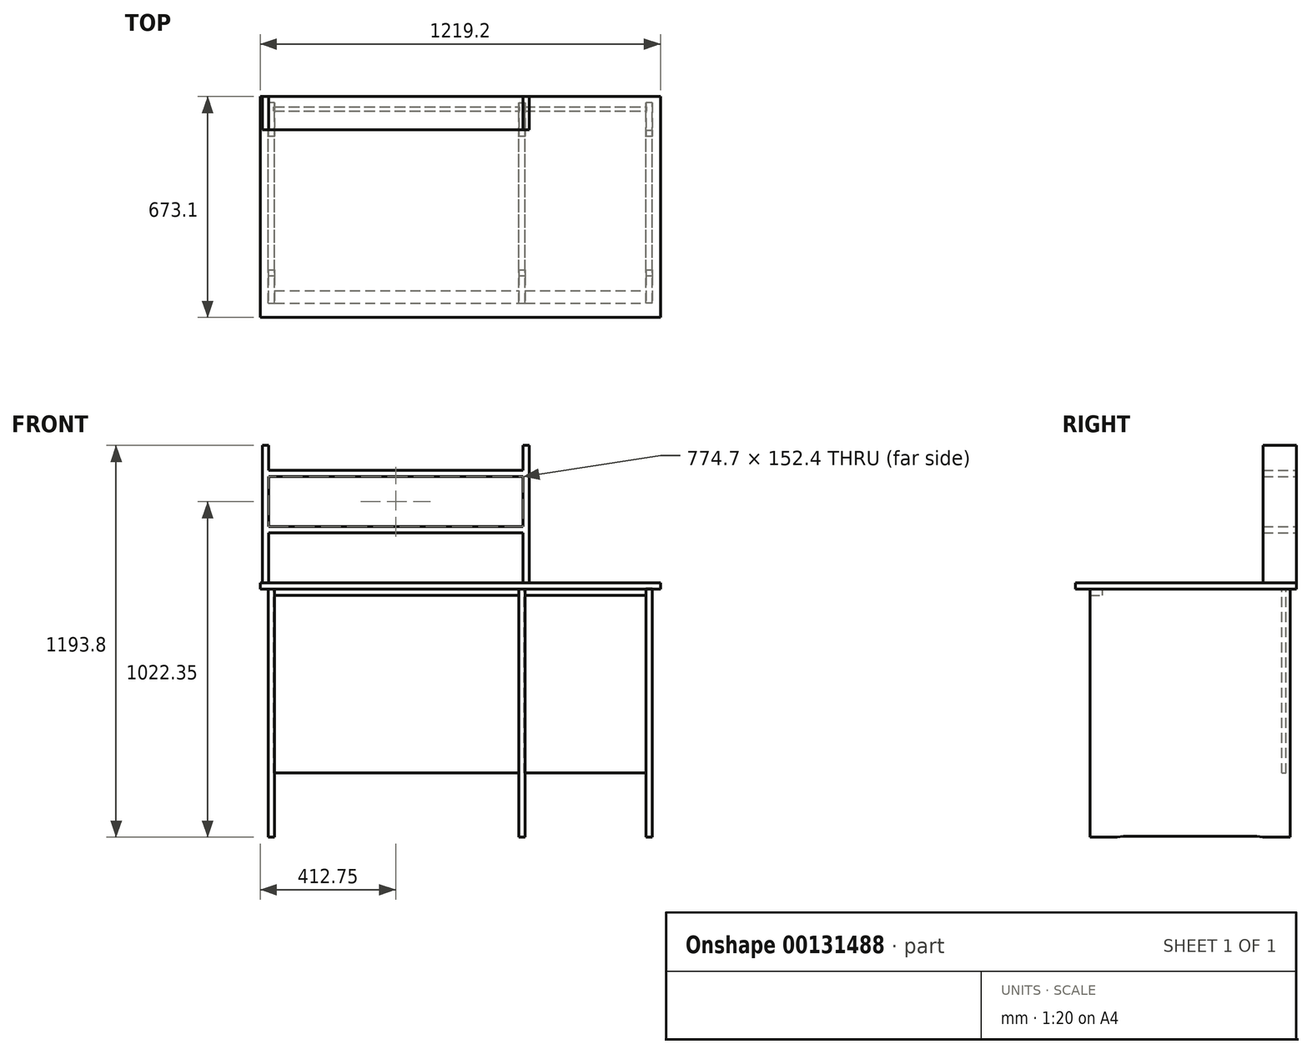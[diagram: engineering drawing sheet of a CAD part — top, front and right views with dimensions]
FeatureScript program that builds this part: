
annotation { "Feature Type Name" : "Feature", "Feature Type Description" : "" }
export const myFeature = defineFeature(function(context is Context, id is Id, definition is map)
    precondition{}
    {
        {
            var Q0;
            Q0=qCreatedBy(makeId("Top.planeOp"),FACE);
            cPlane(context, id + "F0", {"entities" : qUnion([Q0]), "cplaneType" : CPlaneType.OFFSET, "offset" : 774.7 * mm, "width" : 152.4 * mm, "height" : 152.4 * mm});
        }
        {
            var Q0;
            Q0=qCreatedBy(id+"F0.planeOp",FACE);
            var sketch = newSketch(context, id + "F1", { "sketchPlane" : qUnion([Q0])});
            skLineSegment(sketch, "E0.bottom", {"start": v(609.6, 336.55) * mm, "end": v(-609.6, 336.55) * mm});
            skLineSegment(sketch, "E0.top", {"start": v(609.6, -336.55) * mm, "end": v(-609.6, -336.55) * mm});
            skLineSegment(sketch, "E0.left", {"start": v(609.6, 336.55) * mm, "end": v(609.6, -336.55) * mm});
            skLineSegment(sketch, "E0.right", {"start": v(-609.6, 336.55) * mm, "end": v(-609.6, -336.55) * mm});
            skPoint(sketch, "E0.middle", {"position": v(0, 0) * mm});
            skSolve(sketch);
        }
        {
            var Q0;
            Q0 = qSketchRegion(id + "F1", true);
            extrude(context, id + "F2", {"entities" : qUnion([Q0]), "oppositeDirection" : true, "depth" : 19.05 * mm});
        }
        {
            var Q0;
            Q0=makeQuery(id+"F2.opExtrude","CAP_FACE",FACE,{"disambiguationData":[OSD([sQuery(id+"F1.wireOp",EDGE,"E0.bottom"),sQuery(id+"F1.wireOp",EDGE,"E0.top"),sQuery(id+"F1.wireOp",EDGE,"E0.left"),sQuery(id+"F1.wireOp",EDGE,"E0.right")])],"isStart":false});
            var sketch = newSketch(context, id + "F3", { "sketchPlane" : qUnion([Q0])});
            skLineSegment(sketch, "E1.bottom", {"start": v(-584.6, 292.55) * mm, "end": v(-565.6, 292.55) * mm});
            skLineSegment(sketch, "E1.top", {"start": v(-584.6, -317.45) * mm, "end": v(-565.6, -317.45) * mm});
            skLineSegment(sketch, "E1.left", {"start": v(-584.6, 292.55) * mm, "end": v(-584.6, -317.45) * mm});
            skLineSegment(sketch, "E1.right", {"start": v(-565.6, 292.55) * mm, "end": v(-565.6, -317.45) * mm});
            skLineSegment(sketch, "E2.bottom", {"start": v(178.3, 292.55) * mm, "end": v(197.3, 292.55) * mm});
            skLineSegment(sketch, "E2.top", {"start": v(178.3, -317.45) * mm, "end": v(197.3, -317.45) * mm});
            skLineSegment(sketch, "E2.left", {"start": v(178.3, 292.55) * mm, "end": v(178.3, -317.45) * mm});
            skLineSegment(sketch, "E2.right", {"start": v(197.3, 292.55) * mm, "end": v(197.3, -317.45) * mm});
            skLineSegment(sketch, "E3.bottom", {"start": v(584.6, 292.55) * mm, "end": v(565.6, 292.55) * mm});
            skLineSegment(sketch, "E3.top", {"start": v(584.6, -317.45) * mm, "end": v(565.6, -317.45) * mm});
            skLineSegment(sketch, "E3.left", {"start": v(584.6, 292.55) * mm, "end": v(584.6, -317.45) * mm});
            skLineSegment(sketch, "E3.right", {"start": v(565.6, 292.55) * mm, "end": v(565.6, -317.45) * mm});
            skSolve(sketch);
        }
        {
            var Q0;
            Q0 = qSketchRegion(id + "F3", true);
            var Q1;
            Q1=qCreatedBy(makeId("Top.planeOp"),FACE);
            extrude(context, id + "F4", {"entities" : qUnion([Q0]), "endBound" : BoundingType.UP_TO_SURFACE, "endBoundEntityFace" : qUnion([Q1]), "depth" : 25.4 * mm, "hasSecondDirection" : true, "secondDirectionOppositeDirection" : true, "secondDirectionDepth" : 3 * mm});
        }
        {
            var Q0;
            Q0=makeQuery(id+"F2.opExtrude","CAP_FACE",FACE,{"disambiguationData":[OSD([sQuery(id+"F1.wireOp",EDGE,"E0.bottom"),sQuery(id+"F1.wireOp",EDGE,"E0.top"),sQuery(id+"F1.wireOp",EDGE,"E0.left"),sQuery(id+"F1.wireOp",EDGE,"E0.right")])],"isStart":false});
            var sketch = newSketch(context, id + "F5", { "sketchPlane" : qUnion([Q0])});
            skLineSegment(sketch, "E4.bottom", {"start": v(-568.6, -305.45) * mm, "end": v(181.3, -305.45) * mm});
            skLineSegment(sketch, "E4.top", {"start": v(-568.6, -292.45) * mm, "end": v(181.3, -292.45) * mm});
            skLineSegment(sketch, "E4.left", {"start": v(-568.6, -292.45) * mm, "end": v(-568.6, -305.45) * mm});
            skLineSegment(sketch, "E4.right", {"start": v(181.3, -292.45) * mm, "end": v(181.3, -305.45) * mm});
            skPoint(sketch, "E5.oppositeSnap0", {"position": v(-193.65, -292.45) * mm});
            skLineSegment(sketch, "E5.bottom", {"start": v(194.3, -305.45) * mm, "end": v(568.6, -305.45) * mm});
            skLineSegment(sketch, "E5.top", {"start": v(194.3, -292.45) * mm, "end": v(568.6, -292.45) * mm});
            skLineSegment(sketch, "E5.left", {"start": v(194.3, -292.45) * mm, "end": v(194.3, -305.45) * mm});
            skLineSegment(sketch, "E5.right", {"start": v(568.6, -292.45) * mm, "end": v(568.6, -305.45) * mm});
            skLineSegment(sketch, "E6.0.0", {"start": v(-565.6, 292.55) * mm, "end": v(-584.6, 292.55) * mm, "construction": true});
            skLineSegment(sketch, "E6.0.1", {"start": v(-584.6, 292.55) * mm, "end": v(-584.6, -317.45) * mm, "construction": true});
            skLineSegment(sketch, "E6.0.2", {"start": v(-584.6, -317.45) * mm, "end": v(-565.6, -317.45) * mm, "construction": true});
            skLineSegment(sketch, "E6.0.3", {"start": v(-565.6, -317.45) * mm, "end": v(-565.6, 292.55) * mm, "construction": true});
            skLineSegment(sketch, "E7.0.0", {"start": v(197.3, 292.55) * mm, "end": v(178.3, 292.55) * mm, "construction": true});
            skLineSegment(sketch, "E7.0.1", {"start": v(178.3, 292.55) * mm, "end": v(178.3, -317.45) * mm, "construction": true});
            skLineSegment(sketch, "E7.0.2", {"start": v(178.3, -317.45) * mm, "end": v(197.3, -317.45) * mm, "construction": true});
            skLineSegment(sketch, "E7.0.3", {"start": v(197.3, -317.45) * mm, "end": v(197.3, 292.55) * mm, "construction": true});
            skLineSegment(sketch, "E8.0.0", {"start": v(584.6, -317.45) * mm, "end": v(584.6, 292.55) * mm, "construction": true});
            skLineSegment(sketch, "E8.0.1", {"start": v(584.6, 292.55) * mm, "end": v(565.6, 292.55) * mm, "construction": true});
            skLineSegment(sketch, "E8.0.2", {"start": v(565.6, 292.55) * mm, "end": v(565.6, -317.45) * mm, "construction": true});
            skLineSegment(sketch, "E8.0.3", {"start": v(565.6, -317.45) * mm, "end": v(584.6, -317.45) * mm, "construction": true});
            skSolve(sketch);
        }
        {
            var Q0;
            {var subQ0=sQuery(id+"F5.wireOp",EDGE,"E6.0.3");var subQ1=sQuery(id+"F5.wireOp",EDGE,"E4.bottom");var subQ2=makeQuery(id+"F5.imprint","INTERSECT",VERTEX,{"derivedFrom":[subQ1,subQ0]});Q0=makeQuery(id+"F5.imprint","IMPRINT",FACE,{"disambiguationData":[TD([[makeQuery(id+"F5.imprint","IMPRINT",EDGE,{"disambiguationData":[TD([[subQ2,-1.0]])],"derivedFrom":subQ1}),1.0]])]});}
            var Q1;
            {var subQ0=sQuery(id+"F5.wireOp",EDGE,"E7.0.3");var subQ1=sQuery(id+"F5.wireOp",EDGE,"E5.bottom");var subQ2=makeQuery(id+"F5.imprint","INTERSECT",VERTEX,{"derivedFrom":[subQ1,subQ0]});Q1=makeQuery(id+"F5.imprint","IMPRINT",FACE,{"disambiguationData":[TD([[makeQuery(id+"F5.imprint","IMPRINT",EDGE,{"disambiguationData":[TD([[subQ2,-1.0]])],"derivedFrom":subQ1}),1.0]])]});}
            extrude(context, id + "F6", {"entities" : qUnion([Q0, Q1]), "depth" : 560 * mm, "hasSecondDirection" : true, "secondDirectionOppositeDirection" : true, "secondDirectionDepth" : 3 * mm});
        }
        {
            var Q0;
            Q0=makeQuery(id+"F4.opExtrude","SWEPT_BODY",BODY,{"disambiguationData":[OSD([sQuery(id+"F3.wireOp",EDGE,"E1.bottom"),sQuery(id+"F3.wireOp",EDGE,"E1.top"),sQuery(id+"F3.wireOp",EDGE,"E1.left"),sQuery(id+"F3.wireOp",EDGE,"E1.right")])]});
            var Q1;
            Q1=makeQuery(id+"F4.opExtrude","SWEPT_BODY",BODY,{"disambiguationData":[OSD([sQuery(id+"F3.wireOp",EDGE,"E2.bottom"),sQuery(id+"F3.wireOp",EDGE,"E2.top"),sQuery(id+"F3.wireOp",EDGE,"E2.left"),sQuery(id+"F3.wireOp",EDGE,"E2.right")])]});
            var Q2;
            Q2=makeQuery(id+"F4.opExtrude","SWEPT_BODY",BODY,{"disambiguationData":[OSD([sQuery(id+"F3.wireOp",EDGE,"E3.bottom"),sQuery(id+"F3.wireOp",EDGE,"E3.top"),sQuery(id+"F3.wireOp",EDGE,"E3.left"),sQuery(id+"F3.wireOp",EDGE,"E3.right")])]});
            var Q3;
            Q3=makeQuery(id+"F6.opExtrude","SWEPT_BODY",BODY,{"disambiguationData":[OSD([sQuery(id+"F5.wireOp",EDGE,"E4.bottom"),sQuery(id+"F5.wireOp",EDGE,"E4.top"),sQuery(id+"F5.wireOp",EDGE,"E5.bottom"),sQuery(id+"F5.wireOp",EDGE,"E5.top"),sQuery(id+"F5.wireOp",EDGE,"E6.0.0"),sQuery(id+"F5.wireOp",EDGE,"E6.0.1"),sQuery(id+"F5.wireOp",EDGE,"E6.0.2"),sQuery(id+"F5.wireOp",EDGE,"E6.0.3"),sQuery(id+"F5.wireOp",EDGE,"E7.0.0"),sQuery(id+"F5.wireOp",EDGE,"E7.0.1"),sQuery(id+"F5.wireOp",EDGE,"E7.0.2"),sQuery(id+"F5.wireOp",EDGE,"E7.0.3"),sQuery(id+"F5.wireOp",EDGE,"E8.0.0"),sQuery(id+"F5.wireOp",EDGE,"E8.0.1"),sQuery(id+"F5.wireOp",EDGE,"E8.0.2"),sQuery(id+"F5.wireOp",EDGE,"E8.0.3")])]});
            var Q4;
            Q4=makeQuery(id+"F2.opExtrude","SWEPT_BODY",BODY,{"disambiguationData":[OSD([sQuery(id+"F1.wireOp",EDGE,"E0.bottom"),sQuery(id+"F1.wireOp",EDGE,"E0.top"),sQuery(id+"F1.wireOp",EDGE,"E0.left"),sQuery(id+"F1.wireOp",EDGE,"E0.right")])]});
            booleanBodies(context, id + "F7", {"operationType" : BooleanOperationType.SUBTRACTION, "tools" : qUnion([Q0, Q1, Q2, Q3]), "targets" : qUnion([Q4]), "keepTools" : true});
        }
        {
            var Q0;
            Q0=makeQuery(id+"F6.opExtrude","SWEPT_BODY",BODY,{"disambiguationData":[OSD([sQuery(id+"F5.wireOp",EDGE,"E4.bottom"),sQuery(id+"F5.wireOp",EDGE,"E4.top"),sQuery(id+"F5.wireOp",EDGE,"E6.0.3"),sQuery(id+"F5.wireOp",EDGE,"E7.0.1")])]});
            var Q1;
            Q1=makeQuery(id+"F6.opExtrude","SWEPT_BODY",BODY,{"disambiguationData":[OSD([sQuery(id+"F5.wireOp",EDGE,"E5.bottom"),sQuery(id+"F5.wireOp",EDGE,"E5.top"),sQuery(id+"F5.wireOp",EDGE,"E7.0.3"),sQuery(id+"F5.wireOp",EDGE,"E8.0.2")])]});
            var Q2;
            Q2=makeQuery(id+"F4.opExtrude","SWEPT_BODY",BODY,{"disambiguationData":[OSD([sQuery(id+"F3.wireOp",EDGE,"E1.bottom"),sQuery(id+"F3.wireOp",EDGE,"E1.top"),sQuery(id+"F3.wireOp",EDGE,"E1.left"),sQuery(id+"F3.wireOp",EDGE,"E1.right")])]});
            var Q3;
            Q3=makeQuery(id+"F4.opExtrude","SWEPT_BODY",BODY,{"disambiguationData":[OSD([sQuery(id+"F3.wireOp",EDGE,"E2.bottom"),sQuery(id+"F3.wireOp",EDGE,"E2.top"),sQuery(id+"F3.wireOp",EDGE,"E2.left"),sQuery(id+"F3.wireOp",EDGE,"E2.right")])]});
            var Q4;
            Q4=makeQuery(id+"F4.opExtrude","SWEPT_BODY",BODY,{"disambiguationData":[OSD([sQuery(id+"F3.wireOp",EDGE,"E3.bottom"),sQuery(id+"F3.wireOp",EDGE,"E3.top"),sQuery(id+"F3.wireOp",EDGE,"E3.left"),sQuery(id+"F3.wireOp",EDGE,"E3.right")])]});
            booleanBodies(context, id + "F8", {"operationType" : BooleanOperationType.SUBTRACTION, "tools" : qUnion([Q0, Q1]), "targets" : qUnion([Q2, Q3, Q4]), "keepTools" : true});
        }
        {
            var Q0;
            Q0=makeQuery(id+"F2.opExtrude","CAP_FACE",FACE,{"disambiguationData":[OSD([sQuery(id+"F1.wireOp",EDGE,"E0.bottom"),sQuery(id+"F1.wireOp",EDGE,"E0.top"),sQuery(id+"F1.wireOp",EDGE,"E0.left"),sQuery(id+"F1.wireOp",EDGE,"E0.right")])],"isStart":false});
            var sketch = newSketch(context, id + "F9", { "sketchPlane" : qUnion([Q0])});
            skLineSegment(sketch, "E9.bottom", {"start": v(-565.6, 292.55) * mm, "end": v(178.3, 292.55) * mm});
            skLineSegment(sketch, "E9.top", {"start": v(-565.6, 254.45) * mm, "end": v(178.3, 254.45) * mm});
            skLineSegment(sketch, "E9.left", {"start": v(-565.6, 292.55) * mm, "end": v(-565.6, 254.45) * mm});
            skLineSegment(sketch, "E9.right", {"start": v(178.3, 292.55) * mm, "end": v(178.3, 254.45) * mm});
            skLineSegment(sketch, "E10.bottom", {"start": v(197.3, 292.55) * mm, "end": v(565.6, 292.55) * mm});
            skLineSegment(sketch, "E10.top", {"start": v(197.3, 254.45) * mm, "end": v(565.6, 254.45) * mm});
            skLineSegment(sketch, "E10.left", {"start": v(197.3, 292.55) * mm, "end": v(197.3, 254.45) * mm});
            skLineSegment(sketch, "E10.right", {"start": v(565.6, 292.55) * mm, "end": v(565.6, 254.45) * mm});
            skSolve(sketch);
        }
        {
            var Q0;
            Q0 = qSketchRegion(id + "F9", true);
            extrude(context, id + "F10", {"entities" : qUnion([Q0]), "depth" : 19.05 * mm});
        }
        {
            var Q0;
            Q0=makeQuery(id+"F2.opExtrude","SWEPT_FACE",FACE,{"disambiguationData":[OSD([sQuery(id+"F1.wireOp",EDGE,"E0.bottom")])]});
            var sketch = newSketch(context, id + "F11", { "sketchPlane" : qUnion([Q0])});
            skLineSegment(sketch, "E11.bottom", {"start": v(603.25, 774.7) * mm, "end": v(584.2, 774.7) * mm});
            skLineSegment(sketch, "E11.top", {"start": v(584.2, 1117.6) * mm, "end": v(-190.5, 1117.6) * mm});
            skLineSegment(sketch, "E11.left", {"start": v(603.25, 774.7) * mm, "end": v(603.25, 1117.6) * mm});
            skLineSegment(sketch, "E11.right", {"start": v(-209.55, 774.7) * mm, "end": v(-209.55, 1117.6) * mm});
            skLineSegment(sketch, "E12.bottom", {"start": v(584.2, 1098.55) * mm, "end": v(-190.5, 1098.55) * mm});
            skLineSegment(sketch, "E12.top", {"start": v(584.2, 946.15) * mm, "end": v(-190.5, 946.15) * mm});
            skLineSegment(sketch, "E12.left", {"start": v(584.2, 1098.55) * mm, "end": v(584.2, 946.15) * mm});
            skLineSegment(sketch, "E12.right", {"start": v(-190.5, 1098.55) * mm, "end": v(-190.5, 946.15) * mm});
            skLineSegment(sketch, "E13.bottom", {"start": v(584.2, 927.1) * mm, "end": v(-190.5, 927.1) * mm});
            skLineSegment(sketch, "E13.left", {"start": v(584.2, 927.1) * mm, "end": v(584.2, 774.7) * mm});
            skLineSegment(sketch, "E13.right", {"start": v(-190.5, 927.1) * mm, "end": v(-190.5, 774.7) * mm});
            skLineSegment(sketch, "E14.trimOffspring", {"start": v(-190.5, 774.7) * mm, "end": v(-209.55, 774.7) * mm});
            skLineSegment(sketch, "E15", {"start": v(242.76, 1117.6) * mm, "end": v(242.76, 1098.55) * mm, "construction": true});
            skLineSegment(sketch, "E16", {"start": v(227.79, 946.15) * mm, "end": v(227.79, 927.1) * mm, "construction": true});
            skLineSegment(sketch, "E17.top", {"start": v(603.25, 1193.8) * mm, "end": v(584.2, 1193.8) * mm});
            skLineSegment(sketch, "E17.left", {"start": v(603.25, 1117.6) * mm, "end": v(603.25, 1193.8) * mm});
            skLineSegment(sketch, "E17.right", {"start": v(584.2, 1117.6) * mm, "end": v(584.2, 1193.8) * mm});
            skLineSegment(sketch, "E18.top", {"start": v(-209.55, 1193.8) * mm, "end": v(-190.5, 1193.8) * mm});
            skLineSegment(sketch, "E18.left", {"start": v(-209.55, 1117.6) * mm, "end": v(-209.55, 1193.8) * mm});
            skLineSegment(sketch, "E18.right", {"start": v(-190.5, 1117.6) * mm, "end": v(-190.5, 1193.8) * mm});
            skSolve(sketch);
        }
        {
            var Q0;
            Q0 = qSketchRegion(id + "F11", true);
            extrude(context, id + "F12", {"entities" : qUnion([Q0]), "oppositeDirection" : true, "depth" : 101.6 * mm});
        }
        {
            var Q0;
            Q0=makeQuery(id+"F4.opExtrude","SWEPT_FACE",FACE,{"disambiguationData":[OSD([sQuery(id+"F3.wireOp",EDGE,"E3.left")])]});
            var sketch = newSketch(context, id + "F13", { "sketchPlane" : qUnion([Q0])});
            skLineSegment(sketch, "E19", {"start": v(-190.95, 3.17) * mm, "end": v(215.85, 3.18) * mm});
            skLineSegment(sketch, "E20", {"start": v(-190.95, 3.17) * mm, "end": v(-208.96, 0) * mm});
            skLineSegment(sketch, "E21", {"start": v(-208.96, 0) * mm, "end": v(233.86, 0) * mm});
            skLineSegment(sketch, "E22", {"start": v(233.86, 0) * mm, "end": v(215.85, 3.17) * mm});
            skSolve(sketch);
        }
        {
            var Q0;
            Q0 = qSketchRegion(id + "F13", true);
            extrude(context, id + "F14", {"entities" : qUnion([Q0]), "operationType" : NewBodyOperationType.REMOVE, "endBound" : BoundingType.THROUGH_ALL, "oppositeDirection" : true, "depth" : 25.4 * mm});
        }
    });
